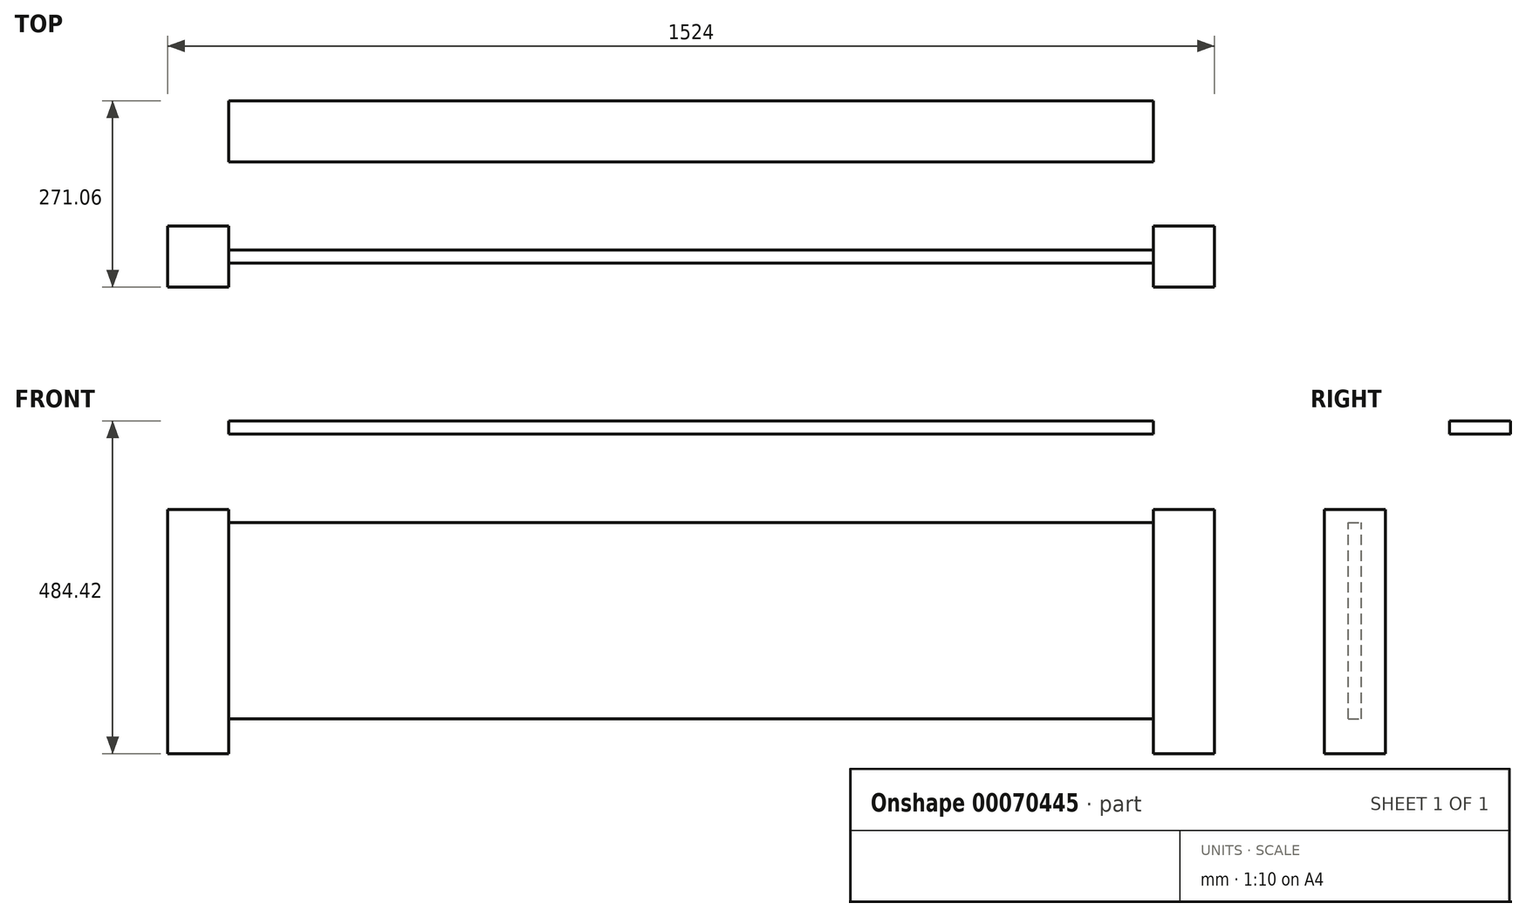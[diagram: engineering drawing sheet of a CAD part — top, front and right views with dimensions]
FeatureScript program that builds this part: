
annotation { "Feature Type Name" : "Feature", "Feature Type Description" : "" }
export const myFeature = defineFeature(function(context is Context, id is Id, definition is map)
    precondition{}
    {
        {
            var Q0;
            Q0=qCreatedBy(makeId("Front.planeOp"),FACE);
            var sketch = newSketch(context, id + "F0", { "sketchPlane" : qUnion([Q0])});
            skLineSegment(sketch, "E0.bottom", {"start": v(-741.2, 252.38) * mm, "end": v(605, 252.38) * mm});
            skLineSegment(sketch, "E0.top", {"start": v(-741.2, -33.37) * mm, "end": v(605, -33.37) * mm});
            skLineSegment(sketch, "E0.left", {"start": v(-741.2, -33.37) * mm, "end": v(-741.2, 252.38) * mm});
            skLineSegment(sketch, "E0.right", {"start": v(605, -33.37) * mm, "end": v(605, 252.38) * mm});
            skSolve(sketch);
        }
        {
            var Q0;
            Q0 = qSketchRegion(id + "F0", true);
            extrude(context, id + "F1", {"entities" : qUnion([Q0]), "depth" : 19.05 * mm});
        }
        {
            var Q0;
            Q0=makeQuery(id+"F1.opExtrude","SWEPT_FACE",FACE,{"disambiguationData":[OSD([sQuery(id+"F0.wireOp",EDGE,"E0.left")])]});
            var sketch = newSketch(context, id + "F2", { "sketchPlane" : qUnion([Q0])});
            skLineSegment(sketch, "E1.bottom", {"start": v(-34.93, 271.43) * mm, "end": v(53.97, 271.43) * mm});
            skLineSegment(sketch, "E1.top", {"start": v(-34.92, -84.17) * mm, "end": v(53.98, -84.17) * mm});
            skLineSegment(sketch, "E1.left", {"start": v(-34.92, 271.43) * mm, "end": v(-34.92, -84.17) * mm});
            skLineSegment(sketch, "E1.right", {"start": v(53.97, 271.43) * mm, "end": v(53.98, -84.17) * mm});
            skSolve(sketch);
        }
        {
            var Q0;
            Q0 = qSketchRegion(id + "F2", true);
            extrude(context, id + "F3", {"entities" : qUnion([Q0]), "depth" : 88.9 * mm});
        }
        {
            var Q0;
            Q0=makeQuery(id+"F1.opExtrude","SWEPT_FACE",FACE,{"disambiguationData":[OSD([sQuery(id+"F0.wireOp",EDGE,"E0.right")])]});
            var sketch = newSketch(context, id + "F4", { "sketchPlane" : qUnion([Q0])});
            skLineSegment(sketch, "E2.bottom", {"start": v(-53.98, 271.43) * mm, "end": v(34.92, 271.43) * mm});
            skLineSegment(sketch, "E2.top", {"start": v(-53.97, -84.17) * mm, "end": v(34.93, -84.17) * mm});
            skLineSegment(sketch, "E2.left", {"start": v(-53.98, 271.43) * mm, "end": v(-53.97, -84.17) * mm});
            skLineSegment(sketch, "E2.right", {"start": v(34.92, 271.43) * mm, "end": v(34.93, -84.17) * mm});
            skSolve(sketch);
        }
        {
            var Q0;
            Q0 = qSketchRegion(id + "F4", true);
            extrude(context, id + "F5", {"entities" : qUnion([Q0]), "depth" : 88.9 * mm});
        }
        {
            var Q0;
            Q0=makeQuery(id+"F5.opExtrude","CAP_FACE",FACE,{"disambiguationData":[OSD([sQuery(id+"F4.wireOp",EDGE,"E2.bottom"),sQuery(id+"F4.wireOp",EDGE,"E2.top"),sQuery(id+"F4.wireOp",EDGE,"E2.left"),sQuery(id+"F4.wireOp",EDGE,"E2.right")])],"isStart":true});
            var sketch = newSketch(context, id + "F6", { "sketchPlane" : qUnion([Q0])});
            skLineSegment(sketch, "E3.bottom", {"start": v(-217.08, 400.25) * mm, "end": v(-128.18, 400.25) * mm});
            skLineSegment(sketch, "E3.top", {"start": v(-217.08, 381.2) * mm, "end": v(-128.18, 381.2) * mm});
            skLineSegment(sketch, "E3.left", {"start": v(-217.08, 400.25) * mm, "end": v(-217.08, 381.2) * mm});
            skLineSegment(sketch, "E3.right", {"start": v(-128.18, 400.25) * mm, "end": v(-128.18, 381.2) * mm});
            skSolve(sketch);
        }
        {
            var Q0;
            Q0 = qSketchRegion(id + "F6", true);
            var Q1;
            Q1=makeQuery(id+"F3.opExtrude","CAP_FACE",FACE,{"disambiguationData":[OSD([sQuery(id+"F2.wireOp",EDGE,"E1.bottom"),sQuery(id+"F2.wireOp",EDGE,"E1.top"),sQuery(id+"F2.wireOp",EDGE,"E1.left"),sQuery(id+"F2.wireOp",EDGE,"E1.right")])],"isStart":true});
            extrude(context, id + "F7", {"entities" : qUnion([Q0]), "endBound" : BoundingType.UP_TO_SURFACE, "endBoundEntityFace" : qUnion([Q1]), "depth" : 25.4 * mm});
        }
    });
